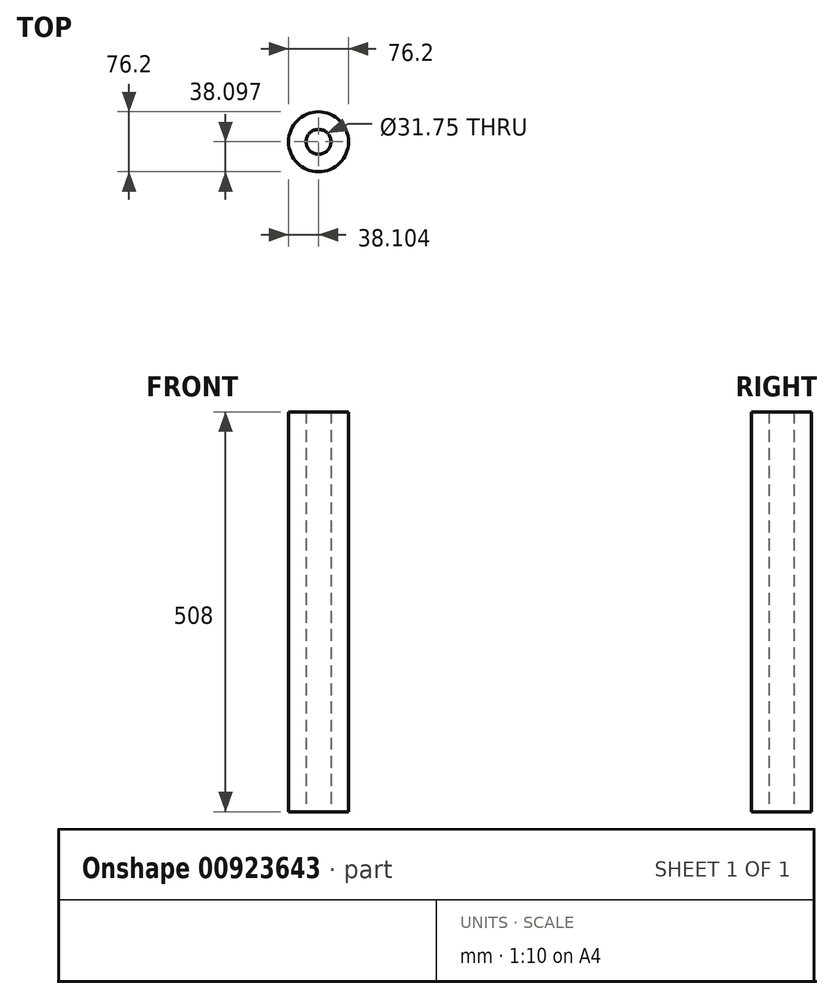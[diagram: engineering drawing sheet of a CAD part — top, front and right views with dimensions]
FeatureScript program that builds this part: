
annotation { "Feature Type Name" : "Feature", "Feature Type Description" : "" }
export const myFeature = defineFeature(function(context is Context, id is Id, definition is map)
    precondition{}
    {
        {
            var Q0;
            Q0=qCreatedBy(makeId("Top.planeOp"),FACE);
            var sketch = newSketch(context, id + "F0", { "sketchPlane" : qUnion([Q0])});
            skCircle(sketch, "E0", {"center": v(-11.03, 6.4) * mm, "radius": 38.1 * mm});
            skCircle(sketch, "E1", {"center": v(-11.03, 6.4) * mm, "radius": 15.88 * mm});
            skSolve(sketch);
        }
        {
            var Q0;
            Q0=qSketchRegion(id+"F0",true);
            extrude(context, id + "F1", {"entities" : qUnion([Q0]), "depth" : 508 * mm});
        }
    });
